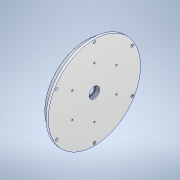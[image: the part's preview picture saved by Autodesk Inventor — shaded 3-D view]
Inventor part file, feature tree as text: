
AUTODESK INVENTOR PART (.ipt)
format: ipt  version: 2020 (Build 240168000, 168)  size: 209,408 bytes
history: native  units: mm
features: sketch x3, chamfer x2, hole x2, revolve x1, pattern_circular x1, projected_geometry x1
ambient origin geometry x8: Origin, YZ Plane, XZ Plane, XY Plane, X Axis, Y Axis, Z Axis, Center Point
bodies: Solid1 (feature_tree)
feature tree (10):
  revolve  "Revolution1"  [1 undecoded]
  chamfer  "Chamfer1"  Distance=6.0mm
  hole  "Hole1"  [1 undecoded]
  pattern_circular  "Circular Pattern1"  Angle=45.0deg  [1 undecoded]
  chamfer  "Chamfer2"  Distance=7.0mm
  hole  "Hole2"  [1 undecoded]
  sketch  "Sketch1"  dims[d6=69.57767mm d7=8.5mm]
  sketch  "Sketch2"  dims[d11=90.0deg]
  projected_geometry  "Projected Loop1"
  sketch  "Sketch3"  dims[d15=1.5mm d17=6.0mm d18=1.625mm d19=1.0mm d20=2.0mm d21=45.0deg d22=7.0mm d23=1.0mm d24=2.0mm d25=64.0mm d26=4.0mm d27=15.0mm d29=4.0mm d30=9.0mm d31=4.5mm d32=4.5mm d33=4.5mm d34=6.0mm d35=9.4mm d36=2.0mm d37=90.0deg d38=8.0mm d39=20.594885mm d40=60.0mm d41=360.0deg d43=0.4mm d44=2.0mm d45=45.0deg d46=90.0mm d47=60.0mm d49=360.0deg d51=2.459mm d52=5.0mm d53=9.4mm d54=2.0mm d55=90.0deg d56=6.5mm d57=20.594885mm]
note: 4 required parameter values undecoded (feature->parameter linkage not recoverable at this tier; creation-order binding heuristic only, values carry confidence <= 0.55)